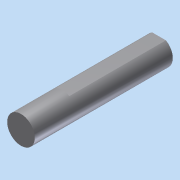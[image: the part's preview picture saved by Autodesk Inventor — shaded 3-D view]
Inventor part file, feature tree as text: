
AUTODESK INVENTOR PART (.ipt)
format: ipt  version: 2012 (Build 160160000, 160)  size: 79,872 bytes
history: native  units: in
note: dims shown in document units (in); Inventor stores cm internally (conversion verified against a paired STEP export)
features: extrude x2, sketch x2
ambient origin geometry x8: Origin, YZ Plane, XZ Plane, XY Plane, X Axis, Y Axis, Z Axis, Center Point
bodies: Solid1 (feature_tree)
feature tree (4):
  extrude  "Extrusion1"  Depth=0.125in
  extrude  "Extrusion2"  Depth=0.375in TaperAngle=0.0deg
  sketch  "Sketch1"  dims[d0=0.25in d1=0.125in]
  sketch  "Sketch2"  dims[d2=1.25in d3=0.0in d4=0.375in d5=0.0in]
